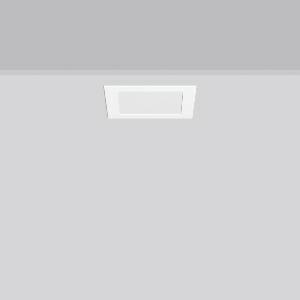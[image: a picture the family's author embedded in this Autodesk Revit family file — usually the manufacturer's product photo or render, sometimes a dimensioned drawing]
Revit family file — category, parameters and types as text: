
# Revit family: toledo_flat_square_e_901486_002_76_5ba2
name_source: partatom
category: Lighting Fixtures
units: mm (PartAtom-declared; Revit-internal decimal feet)

## family parameters
Cut with Voids When Loaded = No
Host = Face
Light Source = No
Part Type = Normal
Room Calculation Point = No
Round Connector Dimension = Use Diameter
Shared = No

## types (1)
- TOLEDO FLAT square E (1 x LED Modul 830, 770 lm, 3000)
    Apparent Load = 8 VA
    CIE Flux Codes = 49 80 96 100 100
    Color Rendering = 80
    Color Temperature = 3000
    Default Elevation = 1800 mm
    Description = Series: TOLEDO FLAT square
Ultra thin recessed downlight. Housing: die-cast aluminium. Light guide and diffuser made of non-yellowing PMMA, opal matt. Ceiling installation with spring system. Mounting depth depends on ceiling strength. Suitable for through-wiring with separately available accessories. Surface mounted housing as accessory for all sizes. Retrofittable decorative cylinders made of chintz fabric as accessory, optional with satin finish plastic diffuser. Through-wiring box (5 pole) available as accessory. 
Colour: white
Length: 172 mm
Width: 172 mm
Height: 3 mm
Cut-out length: 156 mm
Cut-out width: 156 mm
Recess height: 31-56 mm
Luminaire: recess height: 31-51 mm
Lamp: LED
Socket: without socket
Colour temperature: 3000K
Colour rendering index (CRI): 80
System power: 8 W
Rated luminous flux: 770 lm
Luminous efficiency: 96 lm/W
Control gear: Converter, dimmable, DALI
Protection class: II
Type of protection: IP 54
    Height = 0 mm  [stored 0 ft]
    Lamp = 1 x LED Modul 830
    Lamp Light Flux = 770 lm
    Lamp count = 1
    Length = 172 mm
    Lifetime = 50000 h
    Luminous efficacy = 96 lm/W
    Manufacturer = RZB
    ModVariant = No
    Model = 901486.002.76
    Mounting Place = Ceiling
    Mounting Type = Recessed
    Number of Poles = 1
    OnlyDefault = Yes
    Power Factor = 1
    Product Name = TOLEDO FLAT square E
    Product group = Recessed downlights
    ProductGroupID = 402
    Protection Class = Protection class II
    Protection Degree = IP 40
    RLX_Detail_Level = 1
    RLX_Emergency_Light_Flux = 0 lm
    RLX_Emergency_Type = 0
    RLX_Emergency_Type_DB = No
    RlxData = <blob elided: 57741 chars, md5=1c8c39d7>
    Socket = socket
    Standby Power = 0 W
    System Light Flux = 770 lm
    System Power = 8 W
    Type Comments = Product without accessories
    Type Image = 901486.002.jpg
    URL = http://relux.com
    VarID = ---
    Voltage = 230 V
    Voltage Range = 220-240 V
    Weight = 0.00 kg
    Width = 172 mm

note: [stored X ft] marks values corroborated as IEEE doubles in the binary element streams (Revit-internal decimal feet)

## geometry (parser evidence)
native form markers: Blend x4, Sweep x9
no freeform markers — native parametric forms only
